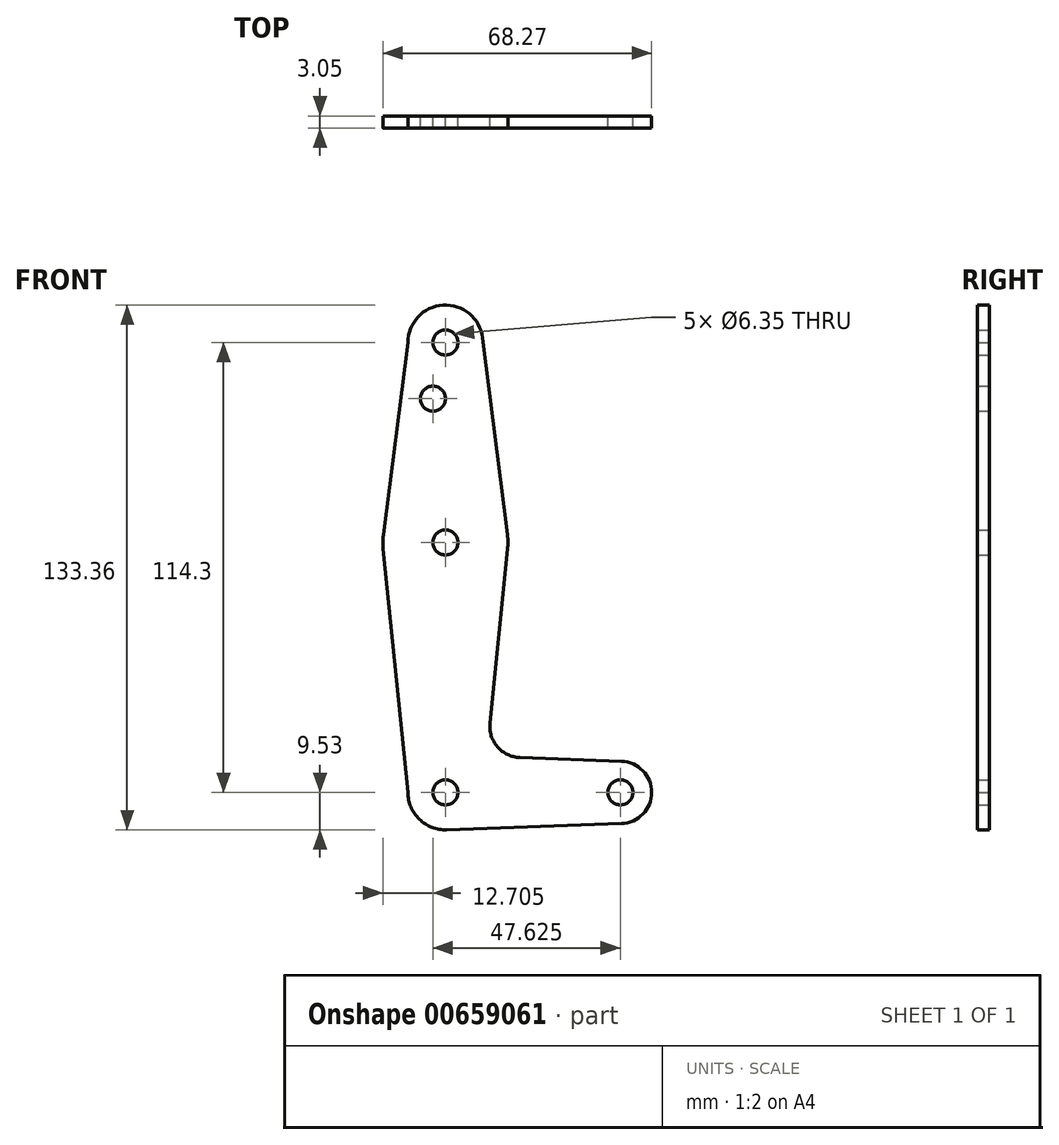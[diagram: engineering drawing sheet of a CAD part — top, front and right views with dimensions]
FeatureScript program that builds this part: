
annotation { "Feature Type Name" : "Feature", "Feature Type Description" : "" }
export const myFeature = defineFeature(function(context is Context, id is Id, definition is map)
    precondition{}
    {
        {
            var Q0;
            Q0=qCreatedBy(makeId("Front.planeOp"),FACE);
            var sketch = newSketch(context, id + "F0", { "sketchPlane" : qUnion([Q0])});
            skCircle(sketch, "E0", {"center": v(0, 114.3) * mm, "radius": 9.53 * mm});
            skCircle(sketch, "E1", {"center": v(0, 63.5) * mm, "radius": 15.88 * mm});
            skCircle(sketch, "E2", {"center": v(0, 0) * mm, "radius": 9.53 * mm});
            skCircle(sketch, "E3", {"center": v(44.45, 0) * mm, "radius": 7.94 * mm});
            skLineSegment(sketch, "E4", {"start": v(0, 114.3) * mm, "end": v(0, 0) * mm, "construction": true});
            skLineSegment(sketch, "E5", {"start": v(0, 0) * mm, "end": v(44.45, 0) * mm, "construction": true});
            skLineSegment(sketch, "E6", {"start": v(-9.53, 114.3) * mm, "end": v(-15.75, 65.5) * mm});
            skLineSegment(sketch, "E7", {"start": v(-9.53, 0) * mm, "end": v(-15.8, 61.9) * mm});
            skLineSegment(sketch, "E8", {"start": v(9.45, 115.5) * mm, "end": v(15.75, 65.48) * mm});
            skLineSegment(sketch, "E9", {"start": v(44.73, -7.93) * mm, "end": v(0, -9.53) * mm});
            skCircle(sketch, "E10", {"center": v(0, 114.3) * mm, "radius": 3.18 * mm});
            skCircle(sketch, "E11", {"center": v(0, 63.5) * mm, "radius": 3.18 * mm});
            skCircle(sketch, "E12", {"center": v(0, 0) * mm, "radius": 3.18 * mm});
            skCircle(sketch, "E13", {"center": v(44.45, 0) * mm, "radius": 3.18 * mm});
            skCircle(sketch, "E14", {"center": v(-3.17, 100.03) * mm, "radius": 3.18 * mm});
            skLineSegment(sketch, "E15", {"start": v(11.3, 17.6) * mm, "end": v(15.8, 61.9) * mm});
            skLineSegment(sketch, "E16", {"start": v(44.73, 7.93) * mm, "end": v(18.93, 8.85) * mm});
            skArc(sketch, "E17.filletArc", {"start": v(11.3, 17.6) * mm, "mid": v(13.22, 11.57) * mm, "end": v(18.93, 8.85) * mm});
            skSolve(sketch);
        }
        {
            var Q0;
            Q0=makeQuery(id+"F0.imprint","IMPRINT",FACE,{"disambiguationData":[TD([[makeQuery(id+"F0.imprint","IMPRINT",EDGE,{"derivedFrom":sQuery(id+"F0.wireOp",EDGE,"E10")}),-1.0]])]});
            var Q1;
            Q1=makeQuery(id+"F0.imprint","IMPRINT",FACE,{"disambiguationData":[TD([[makeQuery(id+"F0.imprint","IMPRINT",EDGE,{"derivedFrom":sQuery(id+"F0.wireOp",EDGE,"E12")}),-1.0]])]});
            var Q2;
            Q2=makeQuery(id+"F0.imprint","IMPRINT",FACE,{"disambiguationData":[TD([[makeQuery(id+"F0.imprint","IMPRINT",EDGE,{"derivedFrom":sQuery(id+"F0.wireOp",EDGE,"E13")}),-1.0]])]});
            var Q3;
            Q3=makeQuery(id+"F0.imprint","IMPRINT",FACE,{"disambiguationData":[TD([[makeQuery(id+"F0.imprint","IMPRINT",EDGE,{"derivedFrom":sQuery(id+"F0.wireOp",EDGE,"E11")}),-1.0]])]});
            var Q4;
            {var subQ0=sQuery(id+"F0.wireOp",EDGE,"E7");Q4=makeQuery(id+"F0.imprint","IMPRINT",FACE,{"disambiguationData":[TD([[makeQuery(id+"F0.imprint","IMPRINT",EDGE,{"derivedFrom":subQ0}),-1.0]])]});}
            var Q5;
            {var subQ0=sQuery(id+"F0.wireOp",EDGE,"E6");Q5=makeQuery(id+"F0.imprint","IMPRINT",FACE,{"disambiguationData":[TD([[makeQuery(id+"F0.imprint","IMPRINT",EDGE,{"derivedFrom":subQ0}),1.0]])]});}
            extrude(context, id + "F1", {"entities" : qUnion([Q0, Q1, Q2, Q3, Q4, Q5]), "depth" : 3.05 * mm, "offsetDistance" : 25.4 * mm});
        }
    });
